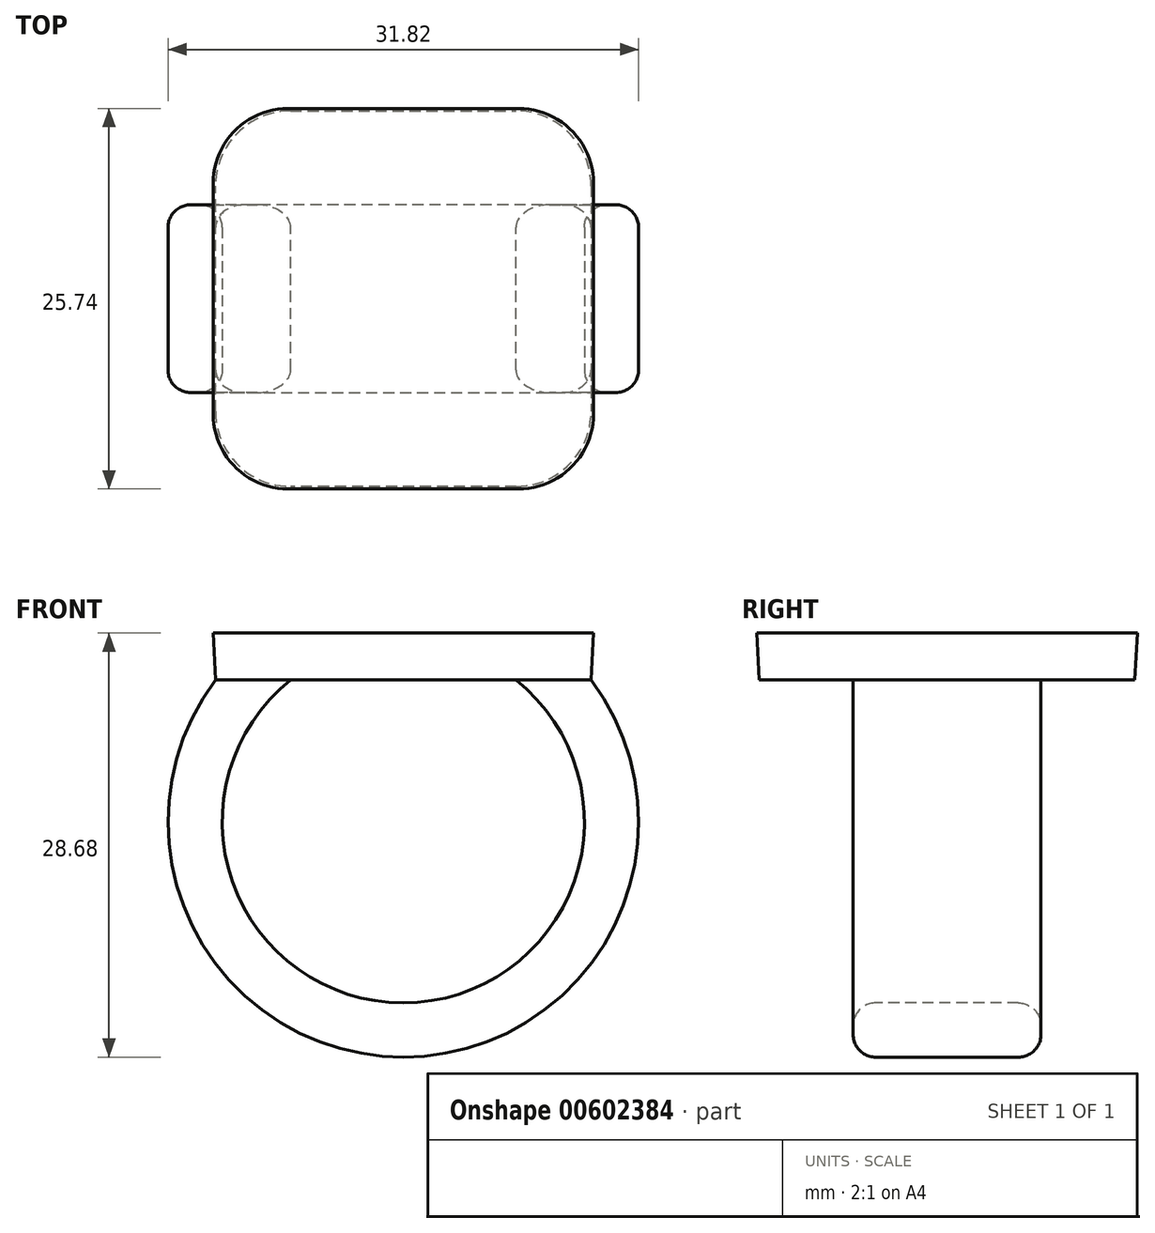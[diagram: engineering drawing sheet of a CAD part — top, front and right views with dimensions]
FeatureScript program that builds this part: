
annotation { "Feature Type Name" : "Feature", "Feature Type Description" : "" }
export const myFeature = defineFeature(function(context is Context, id is Id, definition is map)
    precondition{}
    {
        {
            var Q0;
            Q0=qCreatedBy(makeId("Top.planeOp"),FACE);
            var sketch = newSketch(context, id + "F0", { "sketchPlane" : qUnion([Q0])});
            skLineSegment(sketch, "E0.bottom", {"start": v(12.7, 12.7) * mm, "end": v(-12.7, 12.7) * mm});
            skLineSegment(sketch, "E0.top", {"start": v(12.7, -12.7) * mm, "end": v(-12.7, -12.7) * mm});
            skLineSegment(sketch, "E0.left", {"start": v(12.7, 12.7) * mm, "end": v(12.7, -12.7) * mm});
            skLineSegment(sketch, "E0.right", {"start": v(-12.7, 12.7) * mm, "end": v(-12.7, -12.7) * mm});
            skPoint(sketch, "E0.middle", {"position": v(0, 0) * mm});
            skSolve(sketch);
        }
        {
            var Q0;
            Q0 = qSketchRegion(id + "F0", true);
            extrude(context, id + "F1", {"entities" : qUnion([Q0]), "depth" : 3.17 * mm, "offsetDistance" : 25.4 * mm, "hasDraft" : true, "draftAngle" : 3 * degree});
        }
        {
            var Q0;
            Q0=qCreatedBy(makeId("Front.planeOp"),FACE);
            var sketch = newSketch(context, id + "F2", { "sketchPlane" : qUnion([Q0])});
            skArc(sketch, "E1", {"start": v(-10.16, 0) * mm, "mid": v(0, -23.56) * mm, "end": v(10.16, 0) * mm});
            skSolve(sketch);
        }
        {
            var Q0;
            Q0=makeQuery(id+"F1.opExtrude","CAP_FACE",FACE,{"disambiguationData":[OSD([sQuery(id+"F0.wireOp",EDGE,"E0.bottom"),sQuery(id+"F0.wireOp",EDGE,"E0.top"),sQuery(id+"F0.wireOp",EDGE,"E0.left"),sQuery(id+"F0.wireOp",EDGE,"E0.right")])],"isStart":true});
            var sketch = newSketch(context, id + "F3", { "sketchPlane" : qUnion([Q0])});
            skLineSegment(sketch, "E2.bottom", {"start": v(-7.62, 6.35) * mm, "end": v(-12.7, 6.35) * mm});
            skLineSegment(sketch, "E2.top", {"start": v(-7.62, -6.35) * mm, "end": v(-12.7, -6.35) * mm});
            skLineSegment(sketch, "E2.left", {"start": v(-7.62, 6.35) * mm, "end": v(-7.62, -6.35) * mm});
            skLineSegment(sketch, "E2.right", {"start": v(-12.7, 6.35) * mm, "end": v(-12.7, -6.35) * mm});
            skPoint(sketch, "E2.middle", {"position": v(-10.16, 0) * mm});
            skSolve(sketch);
        }
        {
            var Q0;
            Q0 = qSketchRegion(id + "F3", true);
            var Q1;
            Q1 = qConstructionFilter(qBodyType(qCreatedBy(id + "F2" ,EDGE), BodyType.WIRE), ConstructionObject.NO);
            sweep(context, id + "F4", {"operationType" : NewBodyOperationType.ADD, "profiles" : qUnion([Q0]), "path" : qUnion([Q1])});
        }
        {
            var Q0;
            Q0=qCreatedBy(makeId("Front.planeOp"),FACE);
            var sketch = newSketch(context, id + "F5", { "sketchPlane" : qUnion([Q0])});
            skLineSegment(sketch, "E3.0", {"start": v(10.16, 0) * mm, "end": v(7.62, 0) * mm});
            skArc(sketch, "E3.1", {"start": v(-7.62, 0) * mm, "mid": v(0, -21.84) * mm, "end": v(7.62, 0) * mm});
            skLineSegment(sketch, "E3.2", {"start": v(10.01, -2.54) * mm, "end": v(10.16, 0) * mm});
            skPoint(sketch, "E4.trimOffspring.end.orphan", {"position": v(-12.7, 0) * mm});
            skPoint(sketch, "E5.orphan", {"position": v(12.7, 0) * mm});
            skSolve(sketch);
        }
        {
            var Q0;
            {var subQ0=sQuery(id+"F5.wireOp",EDGE,"E3.0");Q0=makeQuery(id+"F5.imprint","IMPRINT",FACE,{"disambiguationData":[TD([[makeQuery(id+"F5.imprint","IMPRINT",EDGE,{"derivedFrom":subQ0}),1.0]])]});}
            var Q1;
            Q1=makeQuery(id+"F4.opSweep","SWEPT_FACE",FACE,{"disambiguationData":[OSD([sQuery(id+"F2.wireOp",EDGE,"E1"),sQuery(id+"F3.wireOp",EDGE,"E2.bottom")])]});
            var Q2;
            Q2=makeQuery(id+"F4.opSweep","SWEPT_FACE",FACE,{"disambiguationData":[OSD([sQuery(id+"F2.wireOp",EDGE,"E1"),sQuery(id+"F3.wireOp",EDGE,"E2.top")])]});
            extrude(context, id + "F6", {"entities" : qUnion([Q0]), "operationType" : NewBodyOperationType.ADD, "endBound" : BoundingType.UP_TO_SURFACE, "depth" : 25.4 * mm, "endBoundEntityFace" : qUnion([Q1]), "offsetDistance" : 25.4 * mm, "hasSecondDirection" : true, "secondDirectionBound" : SecondDirectionBoundingType.UP_TO_SURFACE, "secondDirectionOppositeDirection" : true, "secondDirectionDepth" : 25.4 * mm, "secondDirectionBoundEntityFace" : qUnion([Q2])});
        }
        {
            var Q0;
            Q0=makeQuery(id+"F1.opExtrude","SWEPT_EDGE",EDGE,{"disambiguationData":[OSD([sQuery(id+"F0.wireOp",EDGE,"E0.top"),sQuery(id+"F0.wireOp",EDGE,"E0.right")])]});
            var Q1;
            Q1=makeQuery(id+"F1.opExtrude","SWEPT_EDGE",EDGE,{"disambiguationData":[OSD([sQuery(id+"F0.wireOp",EDGE,"E0.bottom"),sQuery(id+"F0.wireOp",EDGE,"E0.right")])]});
            var Q2;
            Q2=makeQuery(id+"F1.opExtrude","SWEPT_EDGE",EDGE,{"disambiguationData":[OSD([sQuery(id+"F0.wireOp",EDGE,"E0.bottom"),sQuery(id+"F0.wireOp",EDGE,"E0.left")])]});
            var Q3;
            Q3=makeQuery(id+"F1.opExtrude","SWEPT_EDGE",EDGE,{"disambiguationData":[OSD([sQuery(id+"F0.wireOp",EDGE,"E0.top"),sQuery(id+"F0.wireOp",EDGE,"E0.left")])]});
            fillet(context, id + "F7", {"entities" : qUnion([Q0, Q1, Q2, Q3]), "radius" : 5.08 * mm, "tangentPropagation" : true, "allowEdgeOverflow" : false});
        }
        {
            var Q0;
            Q0=makeQuery(id+"F4.opSweep","SWEPT_EDGE",EDGE,{"disambiguationData":[OSD([sQuery(id+"F0.wireOp",EDGE,"E0.right"),sQuery(id+"F2.wireOp",EDGE,"E1"),sQuery(id+"F3.wireOp",EDGE,"E2.bottom"),sQuery(id+"F3.wireOp",EDGE,"E2.right")])]});
            var Q1;
            {var subQ0=sQuery(id+"F5.wireOp",EDGE,"E3.1");var subQ1=sQuery(id+"F3.wireOp",EDGE,"E2.bottom");var subQ2=sQuery(id+"F2.wireOp",EDGE,"E1");Q1=makeQuery(id+"F6.boolean.opBoolean","MERGE",EDGE,{"derivedFrom":[makeQuery(id+"F4.opSweep","SWEPT_EDGE",EDGE,{"disambiguationData":[OSD([subQ2,subQ1,sQuery(id+"F3.wireOp",EDGE,"E2.left")])]}),makeQuery(id+"F6.opExtrude","TWEAK_EDGE",EDGE,{"derivedFrom":[makeQuery(id+"F4.opSweep","SWEPT_FACE",FACE,{"disambiguationData":[OSD([subQ2,subQ1])]}),makeQuery(id+"F5.imprint","IMPRINT",EDGE,{"disambiguationData":[TD([[makeQuery(id+"F5.imprint","INTERSECT",VERTEX,{"derivedFrom":[sQuery(id+"F5.wireOp",EDGE,"E3.0"),subQ0]}),1.0]])],"derivedFrom":subQ0})]})]});}
            var Q2;
            Q2=makeQuery(id+"F4.opSweep","SWEPT_EDGE",EDGE,{"disambiguationData":[OSD([sQuery(id+"F0.wireOp",EDGE,"E0.right"),sQuery(id+"F2.wireOp",EDGE,"E1"),sQuery(id+"F3.wireOp",EDGE,"E2.top"),sQuery(id+"F3.wireOp",EDGE,"E2.right")])]});
            var Q3;
            {var subQ0=sQuery(id+"F5.wireOp",EDGE,"E3.1");var subQ1=sQuery(id+"F3.wireOp",EDGE,"E2.top");var subQ2=sQuery(id+"F2.wireOp",EDGE,"E1");Q3=makeQuery(id+"F6.boolean.opBoolean","MERGE",EDGE,{"derivedFrom":[makeQuery(id+"F4.opSweep","SWEPT_EDGE",EDGE,{"disambiguationData":[OSD([subQ2,subQ1,sQuery(id+"F3.wireOp",EDGE,"E2.left")])]}),makeQuery(id+"F6.opExtrude","TWEAK_EDGE",EDGE,{"derivedFrom":[makeQuery(id+"F4.opSweep","SWEPT_FACE",FACE,{"disambiguationData":[OSD([subQ2,subQ1])]}),makeQuery(id+"F5.imprint","IMPRINT",EDGE,{"disambiguationData":[TD([[makeQuery(id+"F5.imprint","INTERSECT",VERTEX,{"derivedFrom":[sQuery(id+"F5.wireOp",EDGE,"E3.0"),subQ0]}),1.0]])],"derivedFrom":subQ0})]})]});}
            fillet(context, id + "F8", {"entities" : qUnion([Q0, Q1, Q2, Q3]), "radius" : 1.52 * mm, "tangentPropagation" : true, "allowEdgeOverflow" : false});
        }
    });
